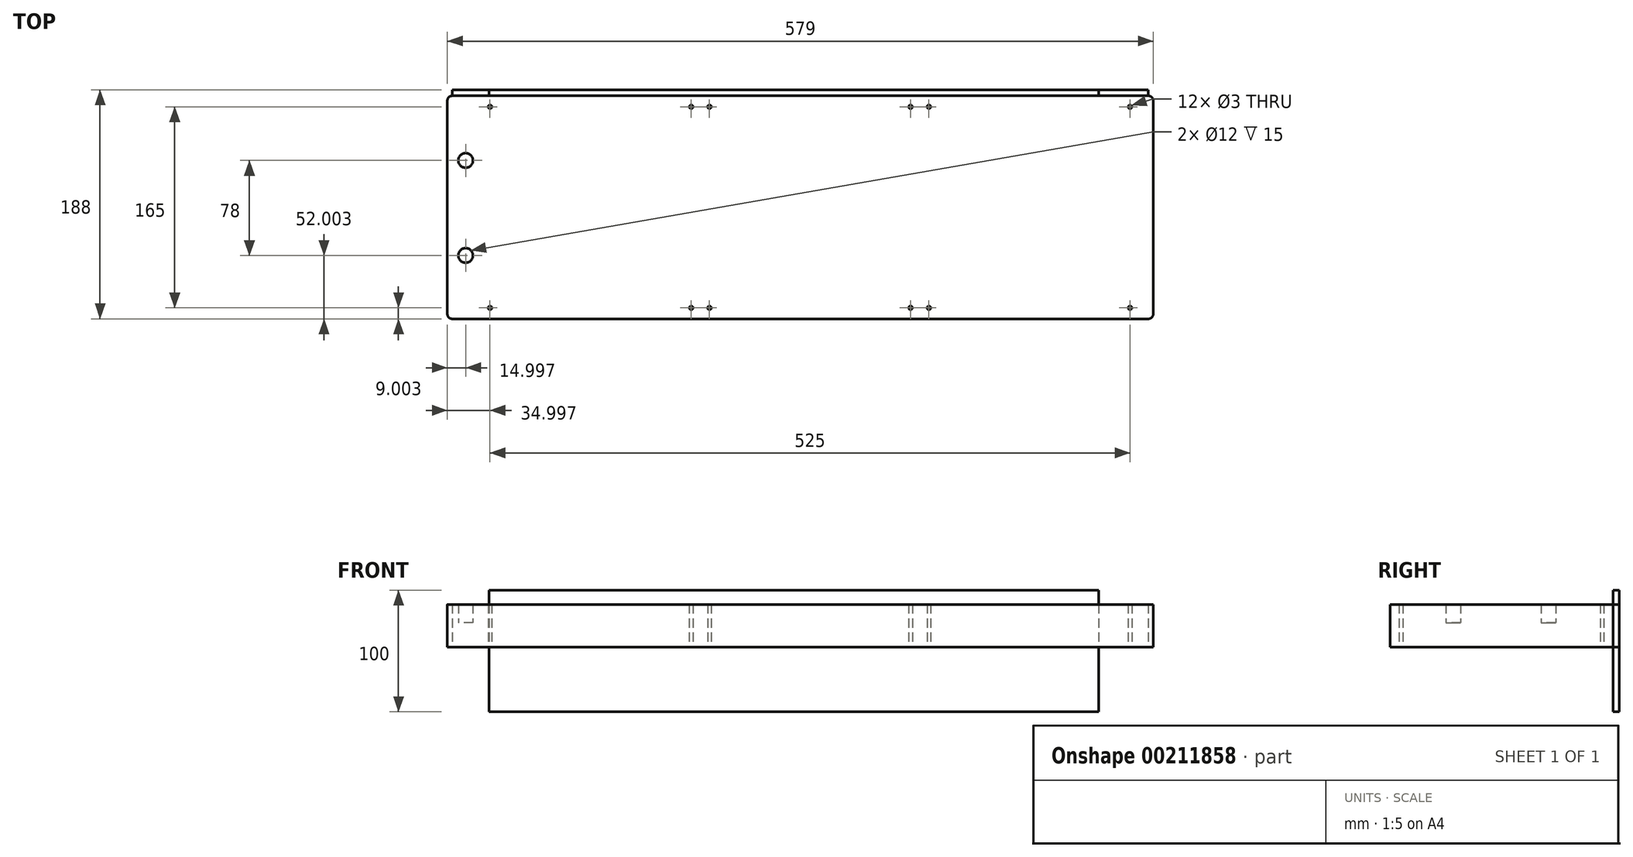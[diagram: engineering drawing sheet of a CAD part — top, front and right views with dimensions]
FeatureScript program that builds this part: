
annotation { "Feature Type Name" : "Feature", "Feature Type Description" : "" }
export const myFeature = defineFeature(function(context is Context, id is Id, definition is map)
    precondition{}
    {
        {
            var Q0;
            Q0=qCreatedBy(makeId("Top.planeOp"),FACE);
            var sketch = newSketch(context, id + "F0", { "sketchPlane" : qUnion([Q0])});
            skLineSegment(sketch, "E0.bottom", {"start": v(-280.87, 53.3) * mm, "end": v(290.13, 53.3) * mm});
            skLineSegment(sketch, "E0.top", {"start": v(-280.87, -129.7) * mm, "end": v(290.13, -129.7) * mm});
            skLineSegment(sketch, "E0.left", {"start": v(-284.87, 49.3) * mm, "end": v(-284.87, -125.7) * mm});
            skLineSegment(sketch, "E0.right", {"start": v(294.13, 49.3) * mm, "end": v(294.13, -125.7) * mm});
            skPoint(sketch, "E1.visualSharp", {"position": v(-284.87, 53.3) * mm});
            skArc(sketch, "E1.filletArc", {"start": v(-280.87, 53.3) * mm, "mid": v(-283.7, 52.13) * mm, "end": v(-284.87, 49.3) * mm});
            skPoint(sketch, "E2.visualSharp", {"position": v(-284.87, -129.7) * mm});
            skArc(sketch, "E2.filletArc", {"start": v(-284.87, -125.7) * mm, "mid": v(-283.7, -128.53) * mm, "end": v(-280.87, -129.7) * mm});
            skPoint(sketch, "E3.visualSharp", {"position": v(294.13, -129.7) * mm});
            skArc(sketch, "E3.filletArc", {"start": v(290.13, -129.7) * mm, "mid": v(292.96, -128.53) * mm, "end": v(294.13, -125.7) * mm});
            skPoint(sketch, "E4.visualSharp", {"position": v(294.13, 53.3) * mm});
            skArc(sketch, "E4.filletArc", {"start": v(294.13, 49.3) * mm, "mid": v(292.96, 52.13) * mm, "end": v(290.13, 53.3) * mm});
            skLineSegment(sketch, "E5", {"start": v(-249.87, 44.3) * mm, "end": v(275.13, 44.3) * mm, "construction": true});
            skLineSegment(sketch, "E6", {"start": v(-249.87, -120.7) * mm, "end": v(275.13, -120.7) * mm, "construction": true});
            skLineSegment(sketch, "E7", {"start": v(-249.87, 44.3) * mm, "end": v(-249.87, -120.7) * mm, "construction": true});
            skLineSegment(sketch, "E8", {"start": v(-84.87, 44.3) * mm, "end": v(-84.87, -120.7) * mm, "construction": true});
            skLineSegment(sketch, "E9", {"start": v(-69.87, 44.3) * mm, "end": v(-69.87, -120.7) * mm, "construction": true});
            skLineSegment(sketch, "E10", {"start": v(95.13, 44.3) * mm, "end": v(95.13, -120.7) * mm, "construction": true});
            skLineSegment(sketch, "E11", {"start": v(110.13, 44.3) * mm, "end": v(110.13, -120.7) * mm, "construction": true});
            skLineSegment(sketch, "E12", {"start": v(275.13, 44.3) * mm, "end": v(275.13, -120.7) * mm, "construction": true});
            skLineSegment(sketch, "E13", {"start": v(235.56, -129.7) * mm, "end": v(235.56, -120.7) * mm, "construction": true});
            skLineSegment(sketch, "E14", {"start": v(235.3, 53.3) * mm, "end": v(235.3, 44.3) * mm, "construction": true});
            skCircle(sketch, "E15", {"center": v(-249.87, 44.3) * mm, "radius": 1.5 * mm});
            skCircle(sketch, "E16", {"center": v(-249.87, -120.7) * mm, "radius": 1.5 * mm});
            skCircle(sketch, "E17", {"center": v(-84.87, -120.7) * mm, "radius": 1.5 * mm});
            skCircle(sketch, "E18", {"center": v(-69.87, -120.7) * mm, "radius": 1.5 * mm});
            skCircle(sketch, "E19", {"center": v(-84.87, 44.3) * mm, "radius": 1.5 * mm});
            skCircle(sketch, "E20", {"center": v(-69.87, 44.3) * mm, "radius": 1.5 * mm});
            skCircle(sketch, "E21", {"center": v(95.13, 44.3) * mm, "radius": 1.5 * mm});
            skCircle(sketch, "E22", {"center": v(110.13, 44.3) * mm, "radius": 1.5 * mm});
            skCircle(sketch, "E23", {"center": v(110.13, -120.7) * mm, "radius": 1.5 * mm});
            skCircle(sketch, "E24", {"center": v(95.13, -120.7) * mm, "radius": 1.5 * mm});
            skCircle(sketch, "E25", {"center": v(275.13, -120.7) * mm, "radius": 1.5 * mm});
            skCircle(sketch, "E26", {"center": v(275.13, 44.3) * mm, "radius": 1.5 * mm});
            skCircle(sketch, "E27", {"center": v(-269.87, 0.3) * mm, "radius": 6 * mm});
            skCircle(sketch, "E28", {"center": v(-269.87, -77.7) * mm, "radius": 6 * mm});
            skLineSegment(sketch, "E29", {"start": v(-269.87, 0.3) * mm, "end": v(-269.87, -77.7) * mm, "construction": true});
            skLineSegment(sketch, "E30", {"start": v(-269.87, 0.3) * mm, "end": v(-269.87, 53.3) * mm, "construction": true});
            skLineSegment(sketch, "E31", {"start": v(-269.87, -77.7) * mm, "end": v(-269.87, -129.7) * mm, "construction": true});
            skSolve(sketch);
        }
        {
            var Q0;
            Q0 = qSketchRegion(id + "F0", true);
            var Q1;
            Q1=makeQuery(id+"F0.imprint","IMPRINT",FACE,{"disambiguationData":[TD([[makeQuery(id+"F0.imprint","IMPRINT",EDGE,{"derivedFrom":sQuery(id+"F0.wireOp",EDGE,"E27")}),1.0]])]});
            var Q2;
            Q2=makeQuery(id+"F0.imprint","IMPRINT",FACE,{"disambiguationData":[TD([[makeQuery(id+"F0.imprint","IMPRINT",EDGE,{"derivedFrom":sQuery(id+"F0.wireOp",EDGE,"E28")}),1.0]])]});
            extrude(context, id + "F1", {"entities" : qUnion([Q0, Q1, Q2]), "depth" : 35 * mm});
        }
        {
            var Q0;
            Q0=makeQuery(id+"F0.imprint","IMPRINT",FACE,{"disambiguationData":[TD([[makeQuery(id+"F0.imprint","IMPRINT",EDGE,{"derivedFrom":sQuery(id+"F0.wireOp",EDGE,"E28")}),1.0]])]});
            var Q1;
            Q1=makeQuery(id+"F0.imprint","IMPRINT",FACE,{"disambiguationData":[TD([[makeQuery(id+"F0.imprint","IMPRINT",EDGE,{"derivedFrom":sQuery(id+"F0.wireOp",EDGE,"E27")}),1.0]])]});
            extrude(context, id + "F2", {"entities" : qUnion([Q0, Q1]), "operationType" : NewBodyOperationType.REMOVE, "depth" : 35 * mm, "hasSecondDirection" : true, "secondDirectionOppositeDirection" : false, "secondDirectionDepth" : 20 * mm});
        }
        {
            var Q0;
            Q0=makeQuery(id+"F1.opExtrude","SWEPT_FACE",FACE,{"disambiguationData":[OSD([sQuery(id+"F0.wireOp",EDGE,"E0.bottom")])]});
            var sketch = newSketch(context, id + "F3", { "sketchPlane" : qUnion([Q0])});
            skLineSegment(sketch, "E32.bottom", {"start": v(280.87, 0) * mm, "end": v(-290.13, 0) * mm});
            skLineSegment(sketch, "E32.top", {"start": v(280.87, 35) * mm, "end": v(-290.13, 35) * mm});
            skLineSegment(sketch, "E32.left", {"start": v(280.87, 0) * mm, "end": v(280.87, 35) * mm});
            skLineSegment(sketch, "E32.right", {"start": v(-290.13, 0) * mm, "end": v(-290.13, 35) * mm});
            skSolve(sketch);
        }
        {
            var Q0;
            Q0 = qSketchRegion(id + "F3", true);
            extrude(context, id + "F4", {"entities" : qUnion([Q0]), "depth" : 5 * mm, "offsetDistance" : 25 * mm});
        }
        {
            var Q0;
            Q0=makeQuery(id+"F1.opExtrude","SWEPT_FACE",FACE,{"disambiguationData":[OSD([sQuery(id+"F0.wireOp",EDGE,"E0.bottom")])]});
            var sketch = newSketch(context, id + "F5", { "sketchPlane" : qUnion([Q0])});
            skLineSegment(sketch, "E33.bottom", {"start": v(-249.47, 46.83) * mm, "end": v(250.53, 46.83) * mm});
            skLineSegment(sketch, "E33.top", {"start": v(-249.47, -53.17) * mm, "end": v(250.53, -53.17) * mm});
            skLineSegment(sketch, "E33.left", {"start": v(-249.47, 46.83) * mm, "end": v(-249.47, -53.17) * mm});
            skLineSegment(sketch, "E33.right", {"start": v(250.53, 46.83) * mm, "end": v(250.53, -53.17) * mm});
            skSolve(sketch);
        }
        {
            var Q0;
            Q0 = qSketchRegion(id + "F5", true);
            extrude(context, id + "F6", {"entities" : qUnion([Q0]), "depth" : 5 * mm, "offsetDistance" : 25 * mm});
        }
    });
